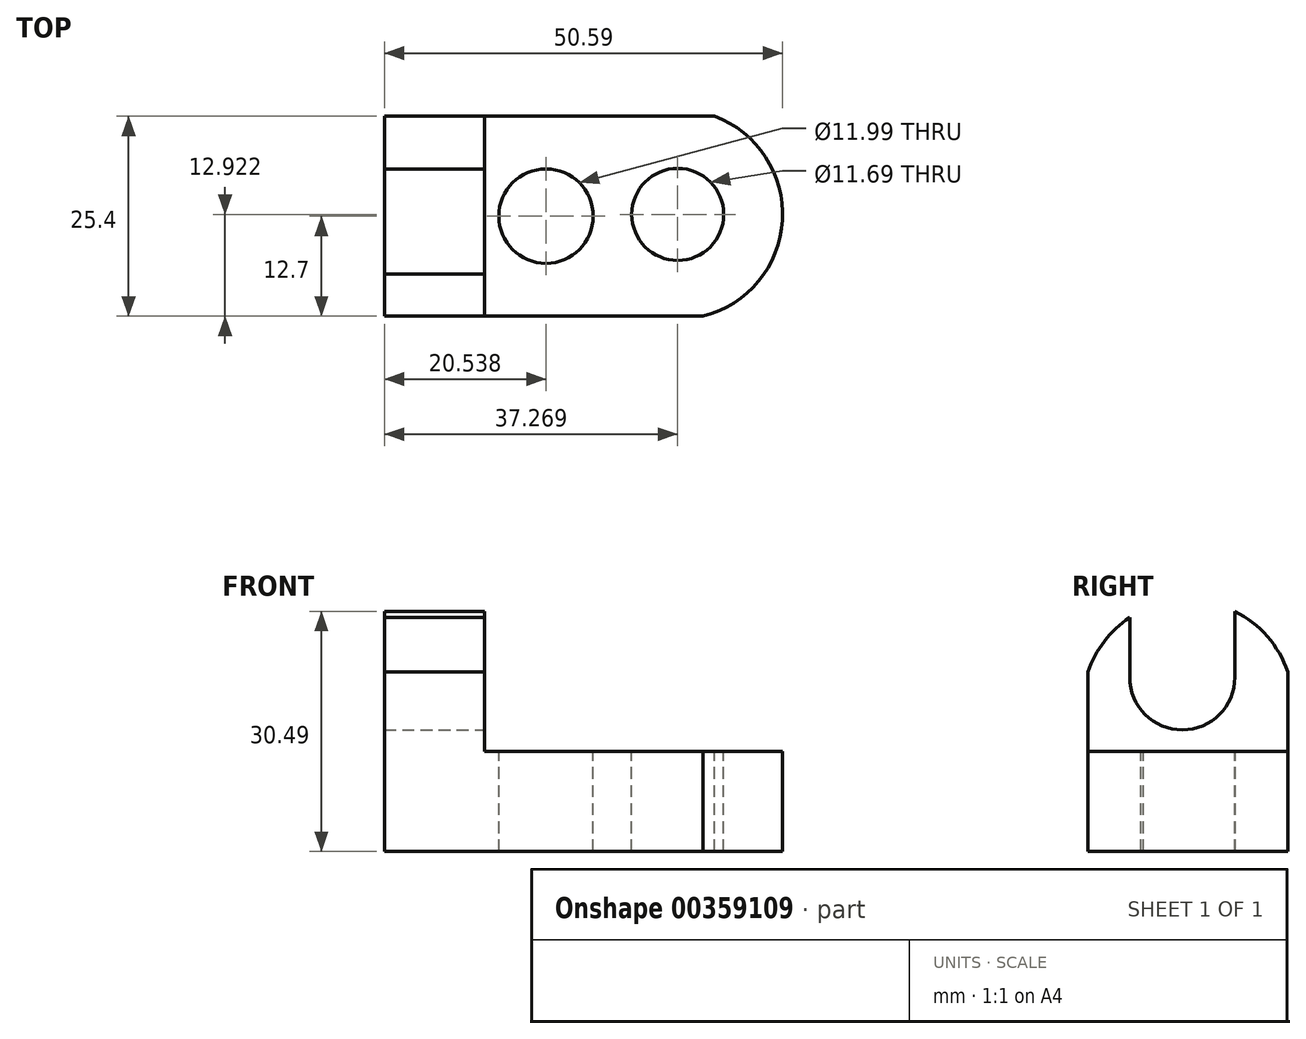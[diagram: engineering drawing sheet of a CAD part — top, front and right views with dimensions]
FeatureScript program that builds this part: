
annotation { "Feature Type Name" : "Feature", "Feature Type Description" : "" }
export const myFeature = defineFeature(function(context is Context, id is Id, definition is map)
    precondition{}
    {
        {
            var Q0;
            Q0=qCreatedBy(makeId("Front.planeOp"),FACE);
            var sketch = newSketch(context, id + "F0", { "sketchPlane" : qUnion([Q0])});
            skLineSegment(sketch, "E0", {"start": v(-70.17, 0) * mm, "end": v(-70.17, 32.86) * mm});
            skLineSegment(sketch, "E1", {"start": v(-70.17, 32.86) * mm, "end": v(-57.47, 32.86) * mm});
            skLineSegment(sketch, "E2", {"start": v(-57.47, 32.86) * mm, "end": v(-57.47, 12.7) * mm});
            skLineSegment(sketch, "E3", {"start": v(-57.47, 12.7) * mm, "end": v(-19.37, 12.7) * mm});
            skLineSegment(sketch, "E4", {"start": v(-19.37, 12.7) * mm, "end": v(-19.37, 0) * mm});
            skLineSegment(sketch, "E5", {"start": v(-19.37, 0) * mm, "end": v(-70.17, 0) * mm});
            skSolve(sketch);
        }
        {
            var Q0;
            Q0 = qSketchRegion(id + "F0", true);
            extrude(context, id + "F1", {"entities" : qUnion([Q0]), "depth" : 25.4 * mm});
        }
        {
            var Q0;
            Q0=makeQuery(id+"F1.opExtrude","SWEPT_FACE",FACE,{"disambiguationData":[OSD([sQuery(id+"F0.wireOp",EDGE,"E2")])]});
            var sketch = newSketch(context, id + "F2", { "sketchPlane" : qUnion([Q0])});
            skArc(sketch, "E6", {"start": v(0, 22.78) * mm, "mid": v(-12.7, 31.9) * mm, "end": v(-25.4, 22.78) * mm});
            skSolve(sketch);
        }
        {
            var Q0;
            {var subQ0=sQuery(id+"F2.wireOp",EDGE,"E6");Q0=makeQuery(id+"F2.imprint","IMPRINT",FACE,{"disambiguationData":[TD([[makeQuery(id+"F2.imprint","IMPRINT",EDGE,{"derivedFrom":subQ0}),-1.0]])]});}
            extrude(context, id + "F3", {"entities" : qUnion([Q0]), "operationType" : NewBodyOperationType.REMOVE, "oppositeDirection" : true, "depth" : 25.4 * mm});
        }
        {
            var Q0;
            Q0=makeQuery(id+"F1.opExtrude","SWEPT_FACE",FACE,{"disambiguationData":[OSD([sQuery(id+"F0.wireOp",EDGE,"E2")])]});
            var sketch = newSketch(context, id + "F4", { "sketchPlane" : qUnion([Q0])});
            skCircle(sketch, "E7", {"center": v(-13.4, 22.1) * mm, "radius": 6.68 * mm});
            skLineSegment(sketch, "E8", {"start": v(-20.08, 22.1) * mm, "end": v(-20.08, 29.68) * mm});
            skLineSegment(sketch, "E9", {"start": v(-6.73, 22.1) * mm, "end": v(-6.73, 30.5) * mm});
            skSolve(sketch);
        }
        {
            var Q0;
            {var subQ0=sQuery(id+"F4.wireOp",EDGE,"E8");Q0=makeQuery(id+"F4.imprint","IMPRINT",FACE,{"disambiguationData":[TD([[makeQuery(id+"F4.imprint","IMPRINT",EDGE,{"derivedFrom":subQ0}),-1.0]])]});}
            var Q1;
            {var subQ0=sQuery(id+"F4.wireOp",EDGE,"E7");var subQ1=makeQuery(id+"F4.imprint","INTERSECT",VERTEX,{"derivedFrom":[subQ0,sQuery(id+"F4.wireOp",EDGE,"E8")]});Q1=makeQuery(id+"F4.imprint","IMPRINT",FACE,{"disambiguationData":[TD([[makeQuery(id+"F4.imprint","IMPRINT",EDGE,{"disambiguationData":[TD([[subQ1,1.0]])],"derivedFrom":subQ0}),1.0]])]});}
            extrude(context, id + "F5", {"entities" : qUnion([Q0, Q1]), "operationType" : NewBodyOperationType.REMOVE, "oppositeDirection" : true, "depth" : 25.4 * mm});
        }
        {
            var Q0;
            Q0=makeQuery(id+"F1.opExtrude","SWEPT_FACE",FACE,{"disambiguationData":[OSD([sQuery(id+"F0.wireOp",EDGE,"E3")])]});
            var sketch = newSketch(context, id + "F6", { "sketchPlane" : qUnion([Q0])});
            skArc(sketch, "E10", {"start": v(-29.67, -25.4) * mm, "mid": v(-19.6, -13.23) * mm, "end": v(-28.24, 0) * mm});
            skSolve(sketch);
        }
        {
            var Q0;
            {var subQ0=sQuery(id+"F6.wireOp",EDGE,"E10");Q0=makeQuery(id+"F6.imprint","IMPRINT",FACE,{"disambiguationData":[TD([[makeQuery(id+"F6.imprint","IMPRINT",EDGE,{"derivedFrom":subQ0}),-1.0]])]});}
            extrude(context, id + "F7", {"entities" : qUnion([Q0]), "operationType" : NewBodyOperationType.REMOVE, "oppositeDirection" : true, "depth" : 25.4 * mm});
        }
        {
            var Q0;
            Q0=makeQuery(id+"F1.opExtrude","SWEPT_FACE",FACE,{"disambiguationData":[OSD([sQuery(id+"F0.wireOp",EDGE,"E3")])]});
            var sketch = newSketch(context, id + "F8", { "sketchPlane" : qUnion([Q0])});
            skCircle(sketch, "E11", {"center": v(-49.63, -12.7) * mm, "radius": 6 * mm});
            skPoint(sketch, "E11.centerSnap0", {"position": v(-57.47, -12.7) * mm});
            skCircle(sketch, "E12", {"center": v(-32.9, -12.48) * mm, "radius": 5.84 * mm});
            skSolve(sketch);
        }
        {
            var Q0;
            Q0=makeQuery(id+"F8.imprint","IMPRINT",FACE,{"disambiguationData":[TD([[makeQuery(id+"F8.imprint","IMPRINT",EDGE,{"derivedFrom":sQuery(id+"F8.wireOp",EDGE,"E12")}),1.0]])]});
            var Q1;
            Q1=makeQuery(id+"F8.imprint","IMPRINT",FACE,{"disambiguationData":[TD([[makeQuery(id+"F8.imprint","IMPRINT",EDGE,{"derivedFrom":sQuery(id+"F8.wireOp",EDGE,"E11")}),1.0]])]});
            extrude(context, id + "F9", {"entities" : qUnion([Q0, Q1]), "operationType" : NewBodyOperationType.REMOVE, "oppositeDirection" : true, "depth" : 25.4 * mm});
        }
    });
